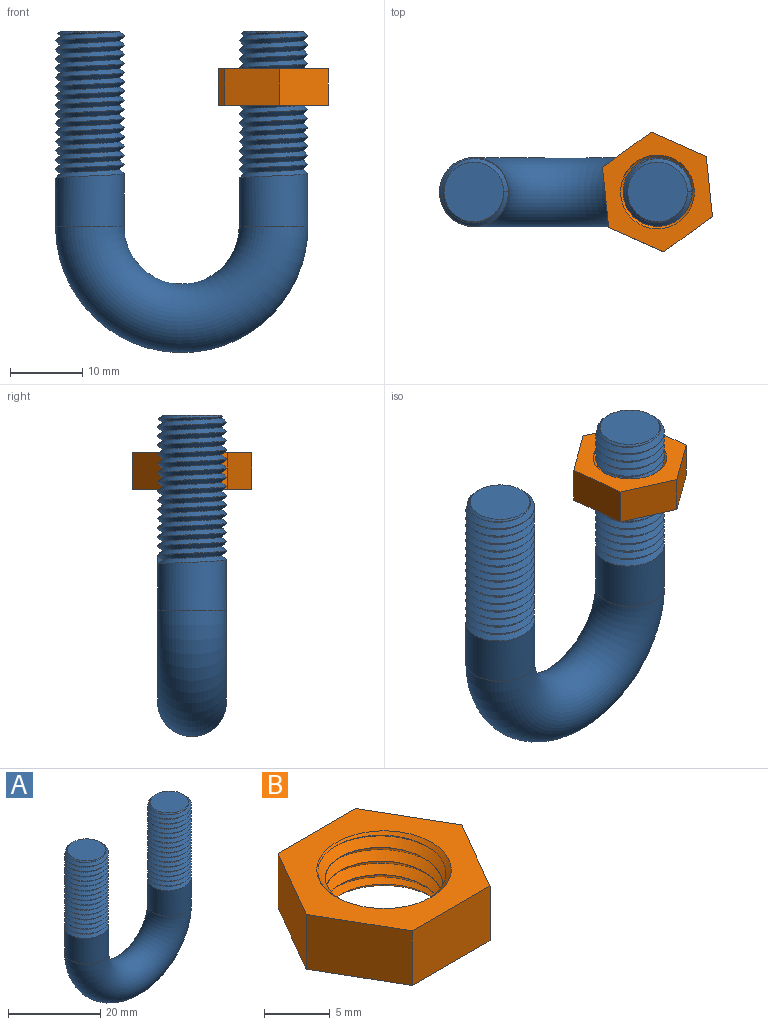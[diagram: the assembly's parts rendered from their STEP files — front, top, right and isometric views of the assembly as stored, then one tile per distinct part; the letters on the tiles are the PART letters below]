
ASSEMBLY  parts=2 mates=1
PART A: 43 faces, bbox 37.8x11x46.5 mm
  f0: plane 8.26x8.26mm, normal (0,0,1), area 53.5mm2, adj f36
  f1: plane 8.26x8.26mm, normal (0,0,1), area 53.5mm2, adj f35
  f2: cylinder r=4.76mm len=9.53mm, axis (0,0,-1), area 209.6mm2, adj f3,f18,f40,f41,f42
  f3: cylinder r=4.76mm len=9.53mm, axis (0,0,-1), area 0.4mm2, adj f2,f4,f41,f42
  f4: cylinder r=4.76mm len=9.53mm, axis (0,0,-1), area 0.4mm2, adj f3,f5,f41,f42
  f5: cylinder r=4.76mm len=9.53mm, axis (0,0,-1), area 0.4mm2, adj f4,f6,f41,f42
  f6: cylinder r=4.76mm len=9.53mm, axis (0,0,-1), area 0.4mm2, adj f5,f7,f41,f42
  f7: cylinder r=4.76mm len=9.53mm, axis (0,0,-1), area 0.4mm2, adj f6,f8,f41,f42
  f8: cylinder r=4.76mm len=9.53mm, axis (0,0,-1), area 0.4mm2, adj f7,f9,f41,f42
  f9: cylinder r=4.76mm len=9.53mm, axis (0,0,-1), area 0.4mm2, adj f8,f10,f41,f42
  f10: cylinder r=4.76mm len=9.53mm, axis (0,0,-1), area 0.4mm2, adj f9,f11,f41,f42
  f11: cylinder r=4.76mm len=9.53mm, axis (0,0,-1), area 0.4mm2, adj f10,f12,f41,f42
  f12: cylinder r=4.76mm len=9.53mm, axis (0,0,-1), area 0.4mm2, adj f11,f13,f41,f42
  f13: cylinder r=4.76mm len=9.53mm, axis (0,0,-1), area 0.4mm2, adj f12,f14,f41,f42
  f14: cylinder r=4.76mm len=9.53mm, axis (0,0,-1), area 0.4mm2, adj f13,f15,f41,f42
  f15: cylinder r=4.76mm len=9.53mm, axis (0,0,-1), area 0.4mm2, adj f14,f16,f41,f42
  f16: cylinder r=4.76mm len=9.53mm, axis (0,0,-1), area 0.4mm2, adj f15,f17,f41,f42
  f17: cylinder r=4.76mm len=9.53mm, axis (0,0,-1), area 0.2mm2, adj f16,f36,f41,f42
  f18: torus R=12.7mm, axis (0,-1,0), area 1193.9mm2, adj f2,f19
  f19: cylinder r=4.76mm len=9.53mm, axis (0,0,1), area 209.7mm2, adj f18,f20,f37,f38,f39
  f20: cylinder r=4.76mm len=9.53mm, axis (0,0,1), area 0.4mm2, adj f19,f21,f38,f39
  f21: cylinder r=4.76mm len=9.53mm, axis (0,0,1), area 0.4mm2, adj f20,f22,f38,f39
  f22: cylinder r=4.76mm len=9.53mm, axis (0,0,1), area 0.4mm2, adj f21,f23,f38,f39
  f23: cylinder r=4.76mm len=9.53mm, axis (0,0,1), area 0.4mm2, adj f22,f24,f38,f39
  f24: cylinder r=4.76mm len=9.53mm, axis (0,0,1), area 0.4mm2, adj f23,f25,f38,f39
  f25: cylinder r=4.76mm len=9.53mm, axis (0,0,1), area 0.4mm2, adj f24,f26,f38,f39
  f26: cylinder r=4.76mm len=9.53mm, axis (0,0,1), area 0.4mm2, adj f25,f27,f38,f39
  f27: cylinder r=4.76mm len=9.53mm, axis (0,0,1), area 0.4mm2, adj f26,f28,f38,f39
  f28: cylinder r=4.76mm len=9.53mm, axis (0,0,1), area 0.4mm2, adj f27,f29,f38,f39
  f29: cylinder r=4.76mm len=9.53mm, axis (0,0,1), area 0.4mm2, adj f28,f30,f38,f39
  f30: cylinder r=4.76mm len=9.53mm, axis (0,0,1), area 0.4mm2, adj f29,f31,f38,f39
  f31: cylinder r=4.76mm len=9.53mm, axis (0,0,1), area 0.4mm2, adj f30,f32,f38,f39
  f32: cylinder r=4.76mm len=9.53mm, axis (0,0,1), area 0.4mm2, adj f31,f33,f38,f39
  f33: cylinder r=4.76mm len=9.53mm, axis (0,0,1), area 0.4mm2, adj f32,f34,f38,f39
  f34: cylinder r=4.76mm len=0.32mm, axis (0,0,1), area 0mm2, adj f33,f35,f39
  f35: cone r=4.13mm half-angle=45deg, axis (0,0,-1), area 12.5mm2, adj f1,f34,f38,f39
  f36: cone r=4.76mm half-angle=45deg, axis (0,0,-1), area 12.5mm2, adj f0,f17,f41,f42
  f37: plane 1.26x0.63mm, normal (-1,-0.01,0), area 0.4mm2, adj f19,f38,f39
  f38: bspline ~20.74x11mm, area 391.5mm2, adj f19,f20,f21,f22,f23,f24,f25,f26
  f39: bspline ~20.74x11mm, area 379mm2, adj f19,f20,f21,f22,f23,f24,f25,f26
  f40: plane 1.26x0.63mm, normal (-1,-0.01,0), area 0.4mm2, adj f2,f41,f42
  f41: bspline ~20.74x11mm, area 391.5mm2, adj f2,f3,f4,f5,f6,f7,f8,f9
  f42: bspline ~20.74x11mm, area 382.1mm2, adj f2,f3,f4,f5,f6,f7,f8,f9
PART B: 13 faces, bbox 16.7x14.4x5.9 mm
  f0: plane 7.22x5.08mm, normal (0.87,0.5,0), area 42.3mm2, adj f1,f5,f7,f8
  f1: plane 8.33x5.08mm, normal (0,1,0), area 42.3mm2, adj f0,f2,f7,f8
  f2: plane 7.22x5.08mm, normal (-0.87,0.5,0), area 42.3mm2, adj f1,f3,f7,f8
  f3: plane 7.22x5.08mm, normal (-0.87,-0.5,0), area 42.3mm2, adj f2,f4,f7,f8
  f4: plane 8.33x5.08mm, normal (0,-1,0), area 42.3mm2, adj f3,f5,f7,f8
  f5: plane 7.22x5.08mm, normal (0.87,-0.5,0), area 42.3mm2, adj f0,f4,f7,f8
  f6: cylinder r=4.47mm len=8.94mm, axis (0,0,-1), area 1mm2, adj f9,f10,f11,f12
  f7: plane 16.67x14.44mm, normal (0,0,1), area 98.6mm2, adj f0,f1,f2,f3,f4,f5,f9
  f8: plane 16.67x14.44mm, normal (0,0,-1), area 98.6mm2, adj f0,f1,f2,f3,f4,f5,f10
  f9: cone r=4.47mm half-angle=45deg, axis (0,0,1), area 14.1mm2, adj f6,f7,f11,f12
  f10: cone r=5.1mm half-angle=45deg, axis (0,0,-1), area 14.1mm2, adj f6,f8,f11,f12
  f11: bspline ~11.77x10.2mm, area 76.5mm2, adj f6,f9,f10,f12
  f12: bspline ~10.2x10.19mm, area 93.7mm2, adj f6,f9,f10,f11
PLACE A at identity fixed
PLACE B rot(axis=(0.98,-0.21,0),180deg) t=(-11.63,-26.1,14.84)mm
MATE cylindrical A.f19 <-> B.f6  axis (0,0,1) through (0,0,20)mm
